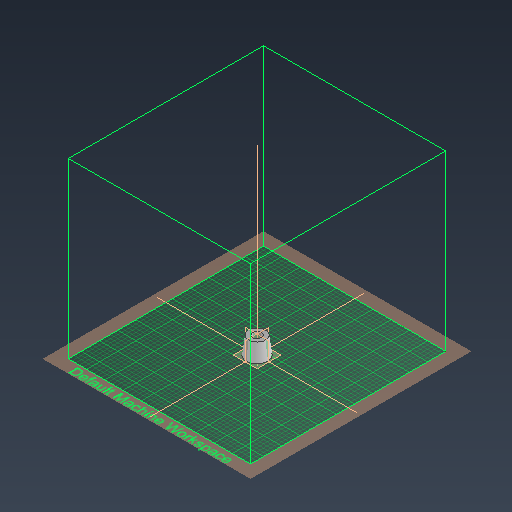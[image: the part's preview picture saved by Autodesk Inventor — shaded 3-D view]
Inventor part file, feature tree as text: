
AUTODESK INVENTOR PART (.ipt)
format: ipt  version: 2021 (Build 250183000, 183)  size: 251,904 bytes
history: native  units: mm
features: sketch x3, plane x1, loft x1, revolve x1
ambient origin geometry x8: Origin, YZ Plane, XZ Plane, XY Plane, X Axis, Y Axis, Z Axis, Center Point
bodies: Solid2 (feature_tree)
feature tree (6):
  sketch  "Sketch1"  dims[d0=50.0mm d14=90.0deg]
  plane  "Work Plane2"
  loft  "Loft2"
  revolve  "Revolution1"  [1 undecoded]
  sketch  "Sketch4"  dims[d15=40.0mm d16=40.0mm]
  sketch  "Sketch5"  dims[d17=0.0mm d18=90.0deg d19=0.0mm d20=90.0deg d22=10.25mm d23=28.0mm d24=6.0mm d26=8.5mm d27=4.75mm]
note: 1 required parameter value undecoded (feature->parameter linkage not recoverable at this tier; creation-order binding heuristic only, values carry confidence <= 0.55)
